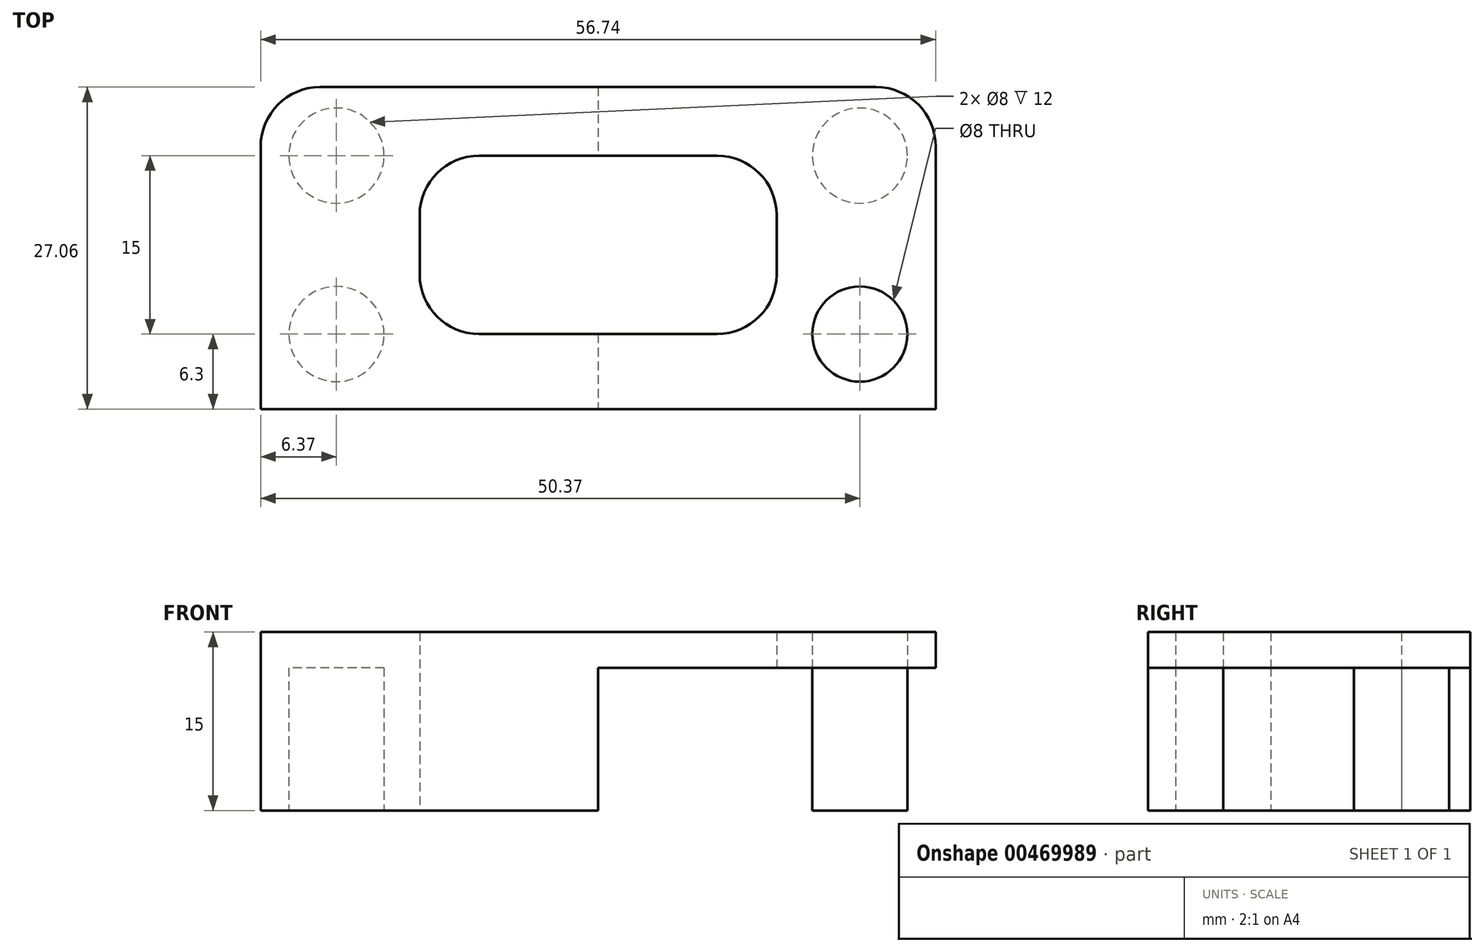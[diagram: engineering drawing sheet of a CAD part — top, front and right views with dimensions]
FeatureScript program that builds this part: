
annotation { "Feature Type Name" : "Feature", "Feature Type Description" : "" }
export const myFeature = defineFeature(function(context is Context, id is Id, definition is map)
    precondition{}
    {
        {
            var Q0;
            Q0=qCreatedBy(makeId("Top.planeOp"),FACE);
            var sketch = newSketch(context, id + "F0", { "sketchPlane" : qUnion([Q0])});
            skLineSegment(sketch, "E0.bottom", {"start": v(0, 0) * mm, "end": v(-30, 0) * mm, "construction": true});
            skLineSegment(sketch, "E0.top", {"start": v(0, 15) * mm, "end": v(-30, 15) * mm, "construction": true});
            skLineSegment(sketch, "E0.left", {"start": v(0, 0) * mm, "end": v(0, 15) * mm, "construction": true});
            skLineSegment(sketch, "E0.right", {"start": v(-30, 0) * mm, "end": v(-30, 15) * mm, "construction": true});
            skLineSegment(sketch, "E1.bottom", {"start": v(0, 15) * mm, "end": v(-22, 15) * mm, "construction": true});
            skLineSegment(sketch, "E1.top", {"start": v(0, 0) * mm, "end": v(-22, 0) * mm, "construction": true});
            skLineSegment(sketch, "E1.left", {"start": v(0, 15) * mm, "end": v(0, 0) * mm, "construction": true});
            skLineSegment(sketch, "E1.right", {"start": v(-22, 15) * mm, "end": v(-22, 0) * mm, "construction": true});
            skCircle(sketch, "E2", {"center": v(-22, 15) * mm, "radius": 4 * mm});
            skCircle(sketch, "E3", {"center": v(-22, 0) * mm, "radius": 4 * mm});
            skLineSegment(sketch, "E4.bottom", {"start": v(0, -6.3) * mm, "end": v(-28.37, -6.3) * mm, "construction": true});
            skLineSegment(sketch, "E4.top", {"start": v(0, 20.76) * mm, "end": v(-28.37, 20.76) * mm, "construction": true});
            skLineSegment(sketch, "E4.left", {"start": v(0, -6.3) * mm, "end": v(0, 20.76) * mm, "construction": true});
            skLineSegment(sketch, "E4.right", {"start": v(-28.37, -6.3) * mm, "end": v(-28.37, 20.76) * mm, "construction": true});
            skLineSegment(sketch, "E5.bottom", {"start": v(0, 20.76) * mm, "end": v(-23.37, 20.76) * mm});
            skLineSegment(sketch, "E5.top", {"start": v(0, -6.3) * mm, "end": v(-28.37, -6.3) * mm});
            skLineSegment(sketch, "E5.left", {"start": v(0, 20.76) * mm, "end": v(0, -6.3) * mm});
            skLineSegment(sketch, "E5.right", {"start": v(-28.37, 15.76) * mm, "end": v(-28.37, -6.3) * mm});
            skCircle(sketch, "E6.MirrorC", {"center": v(22, 15) * mm, "radius": 4 * mm});
            skLineSegment(sketch, "E7.MirrorCS", {"start": v(0, 20.76) * mm, "end": v(23.37, 20.76) * mm});
            skLineSegment(sketch, "E8.MirrorCS", {"start": v(28.37, 15.76) * mm, "end": v(28.37, -6.3) * mm});
            skCircle(sketch, "E9.MirrorC", {"center": v(22, 0) * mm, "radius": 4 * mm});
            skLineSegment(sketch, "E10.MirrorCS", {"start": v(0, -6.3) * mm, "end": v(28.37, -6.3) * mm});
            skLineSegment(sketch, "E11.bottom", {"start": v(0, 0) * mm, "end": v(-10, 0) * mm});
            skLineSegment(sketch, "E11.top", {"start": v(0, 15) * mm, "end": v(-10, 15) * mm});
            skLineSegment(sketch, "E11.left", {"start": v(0, 0) * mm, "end": v(0, 15) * mm});
            skLineSegment(sketch, "E11.right", {"start": v(-15, 5) * mm, "end": v(-15, 10) * mm});
            skPoint(sketch, "E12.visualSharp", {"position": v(-15, 15) * mm});
            skArc(sketch, "E12.filletArc", {"start": v(-10, 15) * mm, "mid": v(-13.54, 13.54) * mm, "end": v(-15, 10) * mm});
            skPoint(sketch, "E13.visualSharp", {"position": v(-15, 0) * mm});
            skArc(sketch, "E13.filletArc", {"start": v(-15, 5) * mm, "mid": v(-13.54, 1.46) * mm, "end": v(-10, 0) * mm});
            skPoint(sketch, "E14.visualSharp", {"position": v(-28.37, 20.76) * mm});
            skArc(sketch, "E14.filletArc", {"start": v(-23.37, 20.76) * mm, "mid": v(-26.9, 19.3) * mm, "end": v(-28.37, 15.76) * mm});
            skPoint(sketch, "E15.visualSharp", {"position": v(28.37, 20.76) * mm});
            skArc(sketch, "E15.filletArc", {"start": v(28.37, 15.76) * mm, "mid": v(26.9, 19.3) * mm, "end": v(23.37, 20.76) * mm});
            skLineSegment(sketch, "E16.MirrorCS", {"start": v(0, 15) * mm, "end": v(10, 15) * mm});
            skArc(sketch, "E17.MirrorCS", {"start": v(10, 15) * mm, "mid": v(13.54, 13.54) * mm, "end": v(15, 10) * mm});
            skLineSegment(sketch, "E18.MirrorCS", {"start": v(15, 5) * mm, "end": v(15, 10) * mm});
            skArc(sketch, "E19.MirrorCS", {"start": v(15, 5) * mm, "mid": v(13.54, 1.46) * mm, "end": v(10, 0) * mm});
            skLineSegment(sketch, "E20.MirrorCS", {"start": v(0, 0) * mm, "end": v(10, 0) * mm});
            skSolve(sketch);
        }
        {
            var Q0;
            Q0=makeQuery(id+"F0.imprint","IMPRINT",FACE,{"disambiguationData":[TD([[makeQuery(id+"F0.imprint","IMPRINT",EDGE,{"derivedFrom":sQuery(id+"F0.wireOp",EDGE,"E2")}),-1.0]])]});
            var Q1;
            Q1=makeQuery(id+"F0.imprint","IMPRINT",FACE,{"disambiguationData":[TD([[makeQuery(id+"F0.imprint","IMPRINT",EDGE,{"derivedFrom":sQuery(id+"F0.wireOp",EDGE,"E6.MirrorC")}),1.0]])]});
            var Q2;
            Q2=makeQuery(id+"F0.imprint","IMPRINT",FACE,{"disambiguationData":[TD([[makeQuery(id+"F0.imprint","IMPRINT",EDGE,{"derivedFrom":sQuery(id+"F0.wireOp",EDGE,"E2")}),1.0]])]});
            var Q3;
            Q3=makeQuery(id+"F0.imprint","IMPRINT",FACE,{"disambiguationData":[TD([[makeQuery(id+"F0.imprint","IMPRINT",EDGE,{"derivedFrom":sQuery(id+"F0.wireOp",EDGE,"E3")}),1.0]])]});
            var Q4;
            Q4=makeQuery(id+"F0.imprint","IMPRINT",FACE,{"disambiguationData":[TD([[makeQuery(id+"F0.imprint","IMPRINT",EDGE,{"derivedFrom":sQuery(id+"F0.wireOp",EDGE,"E6.MirrorC")}),-1.0]])]});
            var Q5;
            Q5=makeQuery(id+"F0.imprint","IMPRINT",FACE,{"disambiguationData":[TD([[makeQuery(id+"F0.imprint","IMPRINT",EDGE,{"derivedFrom":sQuery(id+"F0.wireOp",EDGE,"E9.MirrorC")}),-1.0]])]});
            extrude(context, id + "F1", {"entities" : qUnion([Q0, Q1, Q2, Q3, Q4, Q5]), "depth" : 15 * mm, "offsetDistance" : 25 * mm});
        }
        {
            var Q0;
            Q0=makeQuery(id+"F0.imprint","IMPRINT",FACE,{"disambiguationData":[TD([[makeQuery(id+"F0.imprint","IMPRINT",EDGE,{"derivedFrom":sQuery(id+"F0.wireOp",EDGE,"E6.MirrorC")}),-1.0]])]});
            var Q1;
            Q1=makeQuery(id+"F0.imprint","IMPRINT",FACE,{"disambiguationData":[TD([[makeQuery(id+"F0.imprint","IMPRINT",EDGE,{"derivedFrom":sQuery(id+"F0.wireOp",EDGE,"E9.MirrorC")}),-1.0]])]});
            var Q2;
            Q2=makeQuery(id+"F0.imprint","IMPRINT",FACE,{"disambiguationData":[TD([[makeQuery(id+"F0.imprint","IMPRINT",EDGE,{"derivedFrom":sQuery(id+"F0.wireOp",EDGE,"E2")}),1.0]])]});
            var Q3;
            Q3=makeQuery(id+"F0.imprint","IMPRINT",FACE,{"disambiguationData":[TD([[makeQuery(id+"F0.imprint","IMPRINT",EDGE,{"derivedFrom":sQuery(id+"F0.wireOp",EDGE,"E3")}),1.0]])]});
            extrude(context, id + "F2", {"entities" : qUnion([Q0, Q1, Q2, Q3]), "operationType" : NewBodyOperationType.REMOVE, "depth" : 12 * mm, "offsetDistance" : 25 * mm});
        }
    });
